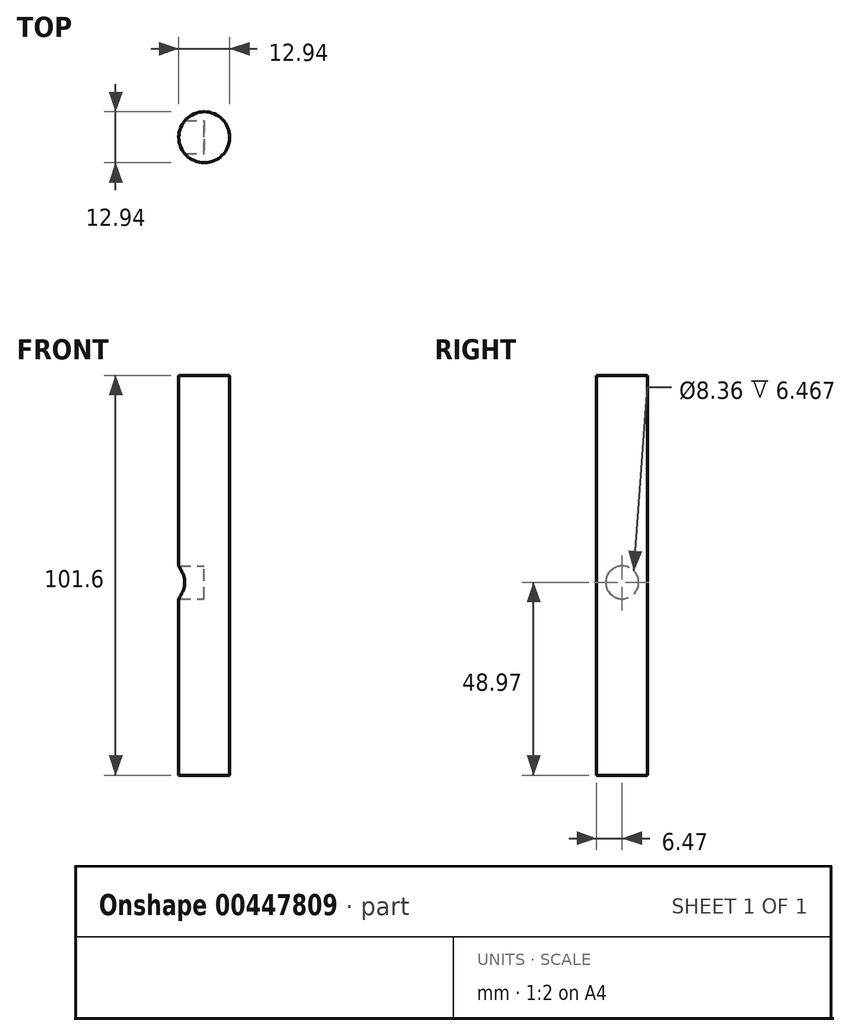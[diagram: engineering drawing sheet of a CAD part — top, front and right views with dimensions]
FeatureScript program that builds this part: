
annotation { "Feature Type Name" : "Feature", "Feature Type Description" : "" }
export const myFeature = defineFeature(function(context is Context, id is Id, definition is map)
    precondition{}
    {
        {
            var Q0;
            Q0=qCreatedBy(makeId("Top.planeOp"),FACE);
            var sketch = newSketch(context, id + "F0", { "sketchPlane" : qUnion([Q0])});
            skCircle(sketch, "E0", {"center": v(0, 0) * mm, "radius": 6.47 * mm});
            skSolve(sketch);
        }
        {
            var Q0;
            Q0=makeQuery(id+"F0.imprint","IMPRINT",FACE,{"disambiguationData":[TD([[makeQuery(id+"F0.imprint","IMPRINT",EDGE,{"derivedFrom":sQuery(id+"F0.wireOp",EDGE,"E0")}),1.0]])]});
            extrude(context, id + "F1", {"entities" : qUnion([Q0]), "depth" : 101.6 * mm});
        }
        {
            var Q0;
            Q0=qCreatedBy(makeId("Right.planeOp"),FACE);
            var sketch = newSketch(context, id + "F2", { "sketchPlane" : qUnion([Q0])});
            skCircle(sketch, "E1", {"center": v(0, 48.97) * mm, "radius": 4.18 * mm});
            skSolve(sketch);
        }
        {
            var Q0;
            Q0 = qSketchRegion(id + "F2", true);
            extrude(context, id + "F3", {"entities" : qUnion([Q0]), "operationType" : NewBodyOperationType.REMOVE, "oppositeDirection" : true, "depth" : 50.8 * mm});
        }
    });
